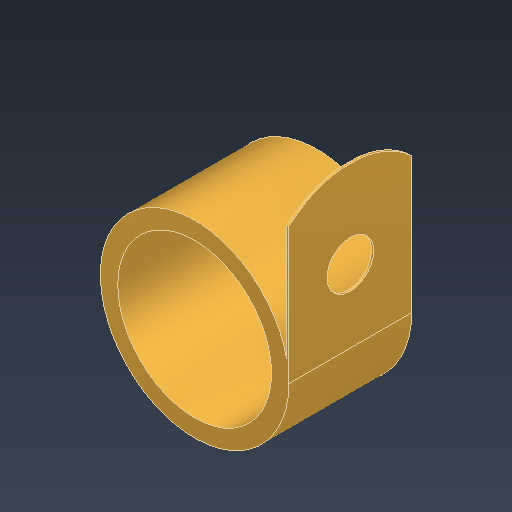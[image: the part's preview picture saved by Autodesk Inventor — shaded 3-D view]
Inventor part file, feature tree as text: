
AUTODESK INVENTOR PART (.ipt)
format: ipt  version: 2021.3 (Build 253353000, 353)  size: 134,656 bytes
history: native  units: mm
features: extrude x2, sketch x2, projected_geometry x1
ambient origin geometry x8: Origin, YZ Plane, XZ Plane, XY Plane, X Axis, Y Axis, Z Axis, Center Point
bodies: Solid1 (feature_tree)
feature tree (5):
  extrude  "Extrusion1"  Depth=0.15mm
  extrude  "Extrusion2"  Depth=8.46mm TaperAngle=0.0deg
  sketch  "Sketch1"  dims[d0=13.0mm d1=0.15mm]
  sketch  "Sketch2"  dims[d2=11.0mm d3=8.46mm d4=0.0mm d5=5.0mm d6=3.22mm d8=4.23mm d9=6.2mm d10=8.46mm d11=0.0mm d12=1.2mm]
  projected_geometry  "Projected Loop1"
